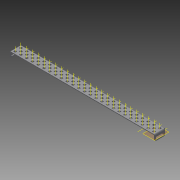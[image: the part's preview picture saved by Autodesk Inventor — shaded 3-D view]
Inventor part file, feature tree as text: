
AUTODESK INVENTOR PART (.ipt)
format: ipt  version: 2015 (Build 190159000, 159)  size: 1,085,952 bytes
history: native  units: in
note: dims shown in document units (in); Inventor stores cm internally (conversion verified against a paired STEP export)
features: other x148, pattern_linear x3, extrude x2, sketch x2, chamfer x1, imported_body x1
ambient origin geometry x8: Origin, YZ Plane, XZ Plane, XY Plane, X Axis, Y Axis, Z Axis, Center Point
bodies: Body1 (feature_tree)
feature tree (157):
  chamfer  "Chamfer2"  Distance=1.0in
  other  "Rail"
  extrude  "left end cut"  Depth=0.5in
  extrude  "length cut"  Depth=0.5in
  other  "top axis"
  other  "inner axis"
  other  "horiz axis"
  pattern_linear  "top axes"  Count1=3 Spacing1=0.5in
  pattern_linear  "inner axes"  Spacing1=0.0in  [1 undecoded]
  pattern_linear  "horiz axes"  Spacing1=0.0in  [1 undecoded]
  other  "slot plane"
  imported_body  "Base1"
  other  "Work Point1"
  other  "Work Point2"
  sketch  "Sketch1"  dims[d3=0.0in d6=0.5in d7=0.7874in d9=0.5in]
  sketch  "Sketch2"  dims[d12=0.5in d15=0.5in d16=1.1811in d18=0.5in d19=0.0in d20=0.0in]
  other  "Work Point3"
  other  "Work Axis4"
  other  "Work Axis5"
  other  "Work Axis6"
  other  "Work Axis7"
  other  "Work Axis8"
  other  "Work Axis9"
  other  "Work Axis10"
  other  "Work Axis11"
  other  "Work Axis12"
  other  "Work Axis13"
  other  "Work Axis14"
  other  "Work Axis15"
  other  "Work Axis16"
  other  "Work Axis17"
  other  "Work Axis18"
  other  "Work Axis19"
  other  "Work Axis20"
  other  "Work Axis21"
  other  "Work Axis22"
  other  "Work Axis23"
  other  "Work Axis24"
  other  "Work Axis25"
  other  "Work Axis26"
  other  "Work Axis27"
  other  "Work Axis28"
  other  "Work Axis29"
  other  "Work Axis30"
  other  "Work Axis31"
  other  "Work Axis32"
  other  "Work Axis33"
  other  "Work Axis34"
  other  "Work Axis35"
  other  "Work Axis36"
  other  "Work Axis37"
  other  "Work Axis38"
  other  "Work Axis39"
  other  "Work Axis40"
  other  "Work Axis41"
  other  "Work Axis42"
  other  "Work Axis43"
  other  "Work Axis44"
  other  "Work Axis45"
  other  "Work Axis46"
  other  "Work Axis47"
  other  "Work Axis48"
  other  "Work Axis49"
  other  "Work Axis50"
  other  "Work Axis51"
  other  "Work Axis52"
  other  "Work Axis53"
  other  "Work Axis144"
  other  "Work Axis145"
  other  "Work Axis146"
  other  "Work Axis147"
  other  "Work Axis148"
  other  "Work Axis149"
  other  "Work Axis150"
  other  "Work Axis151"
  other  "Work Axis152"
  other  "Work Axis153"
  other  "Work Axis154"
  other  "Work Axis155"
  other  "Work Axis156"
  other  "Work Axis157"
  other  "Work Axis158"
  other  "Work Axis159"
  other  "Work Axis160"
  other  "Work Axis161"
  other  "Work Axis162"
  other  "Work Axis163"
  other  "Work Axis164"
  other  "Work Axis165"
  other  "Work Axis166"
  other  "Work Axis167"
  other  "Work Axis168"
  other  "Work Axis169"
  other  "Work Axis170"
  other  "Work Axis171"
  other  "Work Axis172"
  other  "Work Axis173"
  other  "Work Axis174"
  other  "Work Axis175"
  other  "Work Axis176"
  other  "Work Axis177"
  other  "Work Axis178"
  other  "Work Axis179"
  other  "Work Axis180"
  other  "Work Axis181"
  other  "Work Axis182"
  other  "Work Axis183"
  other  "Work Axis184"
  other  "Work Axis185"
  other  "Work Axis186"
  other  "Work Axis187"
  other  "Work Axis188"
  other  "Work Axis189"
  other  "Work Axis190"
  other  "Work Axis191"
  other  "Work Axis192"
  other  "Work Axis193"
  other  "Work Axis194"
  other  "Work Axis195"
  other  "Work Axis196"
  other  "Work Axis197"
  other  "Work Axis198"
  other  "Work Axis199"
  other  "Work Axis200"
  other  "Work Axis201"
  other  "Work Axis202"
  other  "Work Axis203"
  other  "Work Axis204"
  other  "Work Axis205"
  other  "Work Axis206"
  other  "Work Axis207"
  other  "Work Axis208"
  other  "Work Axis209"
  other  "Work Axis210"
  other  "Work Axis211"
  other  "Work Axis212"
  other  "Work Axis213"
  other  "Work Axis214"
  other  "Work Axis215"
  other  "Work Axis216"
  other  "Work Axis217"
  other  "Work Axis218"
  other  "Work Axis219"
  other  "Work Axis220"
  other  "Work Axis221"
  other  "Work Axis222"
  other  "Work Axis223"
  other  "Work Axis224"
  other  "Work Axis225"
  other  "Work Axis226"
  other  "Work Axis227"
  other  "Work Axis228"
  other  "Work Axis229"
  other  "Work Axis230"
  other  "Work Axis231"
  other  "Work Axis232"
  other  "Work Axis233"
note: 2 required parameter values undecoded (feature->parameter linkage not recoverable at this tier; creation-order binding heuristic only, values carry confidence <= 0.55)
